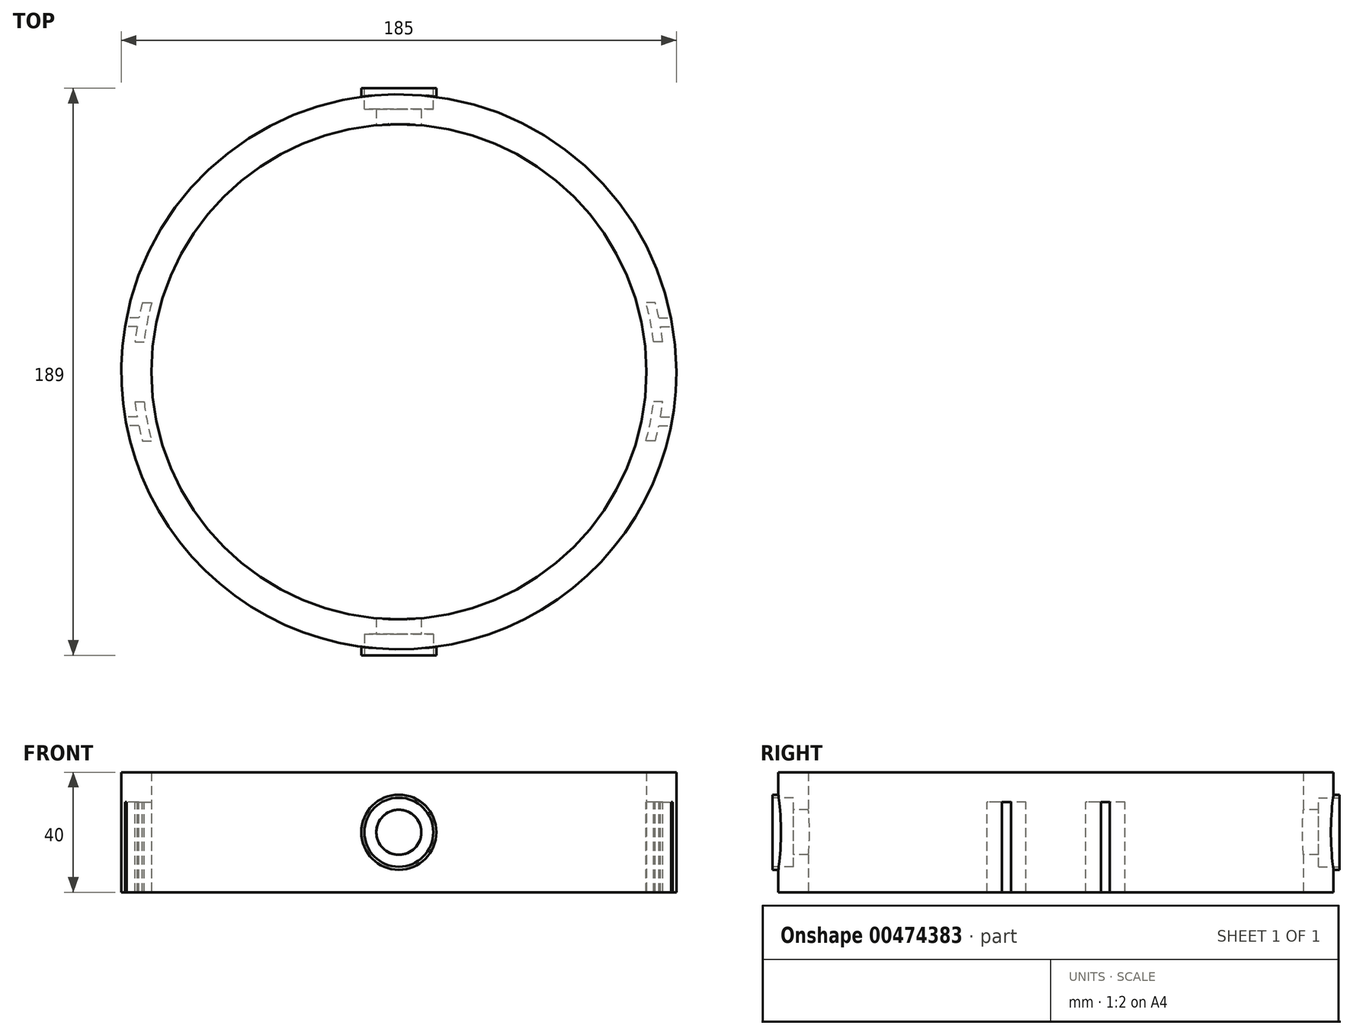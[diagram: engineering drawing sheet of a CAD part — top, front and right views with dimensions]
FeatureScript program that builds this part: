
annotation { "Feature Type Name" : "Feature", "Feature Type Description" : "" }
export const myFeature = defineFeature(function(context is Context, id is Id, definition is map)
    precondition{}
    {
        {
            var Q0;
            Q0=qCreatedBy(makeId("Top.planeOp"),FACE);
            var sketch = newSketch(context, id + "F0", { "sketchPlane" : qUnion([Q0])});
            skCircle(sketch, "E0", {"center": v(0, 0) * mm, "radius": 82.5 * mm});
            skCircle(sketch, "E1", {"center": v(0, 0) * mm, "radius": 92.5 * mm});
            skSolve(sketch);
        }
        {
            var Q0;
            Q0 = qSketchRegion(id + "F0", true);
            extrude(context, id + "F1", {"entities" : qUnion([Q0]), "depth" : 20 * mm, "hasSecondDirection" : true, "secondDirectionOppositeDirection" : true, "secondDirectionDepth" : 20 * mm});
        }
        {
            var Q0;
            Q0=qCreatedBy(makeId("Front.planeOp"),FACE);
            var sketch = newSketch(context, id + "F2", { "sketchPlane" : qUnion([Q0])});
            skCircle(sketch, "E2", {"center": v(0, 0) * mm, "radius": 7.5 * mm});
            skSolve(sketch);
        }
        {
            var Q0;
            Q0 = qSketchRegion(id + "F2", true);
            extrude(context, id + "F3", {"entities" : qUnion([Q0]), "operationType" : NewBodyOperationType.REMOVE, "endBound" : BoundingType.THROUGH_ALL, "oppositeDirection" : true, "depth" : 25 * mm, "hasSecondDirection" : true, "secondDirectionBound" : SecondDirectionBoundingType.THROUGH_ALL, "secondDirectionOppositeDirection" : false, "secondDirectionDepth" : 25 * mm});
        }
        {
            var Q0;
            Q0=qCreatedBy(makeId("Front.planeOp"),FACE);
            cPlane(context, id + "F4", {"entities" : qUnion([Q0]), "cplaneType" : CPlaneType.OFFSET, "offset" : 185 / 2 * mm, "width" : 150 * mm, "height" : 150 * mm});
        }
        {
            var Q0;
            Q0=qCreatedBy(id+"F4.planeOp",FACE);
            var sketch = newSketch(context, id + "F5", { "sketchPlane" : qUnion([Q0])});
            skCircle(sketch, "E3", {"center": v(0, 0) * mm, "radius": 11.5 * mm});
            skSolve(sketch);
        }
        {
            var Q0;
            Q0 = qSketchRegion(id + "F5", true);
            extrude(context, id + "F6", {"entities" : qUnion([Q0]), "operationType" : NewBodyOperationType.REMOVE, "oppositeDirection" : true, "depth" : 5 * mm});
        }
        {
            var Q0;
            Q0=qCreatedBy(makeId("Front.planeOp"),FACE);
            cPlane(context, id + "F7", {"entities" : qUnion([Q0]), "cplaneType" : CPlaneType.OFFSET, "offset" : (185 / 2) * mm, "oppositeDirection" : true, "width" : 150 * mm, "height" : 150 * mm});
        }
        {
            var Q0;
            Q0=qCreatedBy(id+"F7.planeOp",FACE);
            var sketch = newSketch(context, id + "F8", { "sketchPlane" : qUnion([Q0])});
            skCircle(sketch, "E4", {"center": v(0, 0) * mm, "radius": 11.5 * mm});
            skSolve(sketch);
        }
        {
            var Q0;
            Q0 = qSketchRegion(id + "F8", true);
            extrude(context, id + "F9", {"entities" : qUnion([Q0]), "operationType" : NewBodyOperationType.REMOVE, "depth" : 5 * mm});
        }
        {
            var Q0;
            Q0=qCreatedBy(id+"F4.planeOp",FACE);
            var sketch = newSketch(context, id + "F10", { "sketchPlane" : qUnion([Q0])});
            skCircle(sketch, "E5.0", {"center": v(0, 0) * mm, "radius": 11.5 * mm});
            skCircle(sketch, "E6", {"center": v(0, 0) * mm, "radius": 12.5 * mm});
            skSolve(sketch);
        }
        {
            var Q0;
            Q0 = qSketchRegion(id + "F10", true);
            var Q1;
            Q1=makeQuery(id+"F1.opExtrude","SWEPT_FACE",FACE,{"disambiguationData":[OSD([sQuery(id+"F0.wireOp",EDGE,"E1")])]});
            extrude(context, id + "F11", {"entities" : qUnion([Q0]), "operationType" : NewBodyOperationType.ADD, "depth" : 2 * mm, "hasSecondDirection" : true, "secondDirectionBound" : SecondDirectionBoundingType.UP_TO_SURFACE, "secondDirectionOppositeDirection" : true, "secondDirectionBoundEntityFace" : qUnion([Q1]), "secondDirectionDepth" : 25 * mm});
        }
        {
            var Q0;
            Q0=qCreatedBy(id+"F7.planeOp",FACE);
            var sketch = newSketch(context, id + "F12", { "sketchPlane" : qUnion([Q0])});
            skCircle(sketch, "E7", {"center": v(0, 0) * mm, "radius": 12.5 * mm});
            skCircle(sketch, "E8.0", {"center": v(0, 0) * mm, "radius": 11.5 * mm});
            skSolve(sketch);
        }
        {
            var Q0;
            Q0 = qSketchRegion(id + "F12", true);
            extrude(context, id + "F13", {"entities" : qUnion([Q0]), "operationType" : NewBodyOperationType.ADD, "oppositeDirection" : true, "depth" : 2 * mm, "hasSecondDirection" : true, "secondDirectionBound" : SecondDirectionBoundingType.UP_TO_NEXT, "secondDirectionOppositeDirection" : false, "secondDirectionDepth" : 25 * mm});
        }
        {
            var Q0;
            Q0=qCreatedBy(makeId("Top.planeOp"),FACE);
            var sketch = newSketch(context, id + "F14", { "sketchPlane" : qUnion([Q0])});
            skArc(sketch, "E9.0", {"start": v(-91.28, -15) * mm, "mid": v(-91.02, -16.5) * mm, "end": v(-90.73, -18) * mm});
            skCircle(sketch, "E10.0", {"center": v(0, 0) * mm, "radius": 82.5 * mm, "construction": true});
            skArc(sketch, "E11", {"start": v(-86.65, -18) * mm, "mid": v(-86.1, -20.5) * mm, "end": v(-85.46, -23) * mm});
            skArc(sketch, "E12", {"start": v(-84.91, -10) * mm, "mid": v(-83.88, -16.55) * mm, "end": v(-82.35, -23) * mm});
            skLineSegment(sketch, "E13", {"start": v(0, 0) * mm, "end": v(-131.44, 0) * mm, "construction": true});
            skLineSegment(sketch, "E14", {"start": v(-86.65, -18) * mm, "end": v(-90.73, -18) * mm});
            skLineSegment(sketch, "E15", {"start": v(-87.22, -15) * mm, "end": v(-91.28, -15) * mm});
            skLineSegment(sketch, "E16.MirrorCS", {"start": v(-86.65, 18) * mm, "end": v(-90.73, 18) * mm});
            skLineSegment(sketch, "E17.MirrorCS", {"start": v(-87.22, 15) * mm, "end": v(-91.28, 15) * mm});
            skLineSegment(sketch, "E18", {"start": v(-85.46, -23) * mm, "end": v(-82.35, -23) * mm});
            skLineSegment(sketch, "E19", {"start": v(-87.93, -10) * mm, "end": v(-84.91, -10) * mm});
            skLineSegment(sketch, "E20.MirrorCS", {"start": v(-87.93, 10) * mm, "end": v(-84.91, 10) * mm});
            skLineSegment(sketch, "E21.MirrorCS", {"start": v(-85.46, 23) * mm, "end": v(-82.35, 23) * mm});
            skArc(sketch, "E22.trimOffspring", {"start": v(-87.22, 15) * mm, "mid": v(-87.61, 12.5) * mm, "end": v(-87.93, 10) * mm});
            skArc(sketch, "E23.trimOffspring", {"start": v(-87.93, -10) * mm, "mid": v(-87.61, -12.5) * mm, "end": v(-87.22, -15) * mm});
            skArc(sketch, "E24.trimOffspring", {"start": v(-82.35, 23) * mm, "mid": v(-83.88, 16.55) * mm, "end": v(-84.91, 10) * mm});
            skArc(sketch, "E25.trimOffspring", {"start": v(-85.46, 23) * mm, "mid": v(-86.1, 20.5) * mm, "end": v(-86.65, 18) * mm});
            skLineSegment(sketch, "E26.1.0", {"start": v(86.65, 18) * mm, "end": v(90.73, 18) * mm});
            skLineSegment(sketch, "E26.1.1", {"start": v(85.46, 23) * mm, "end": v(82.35, 23) * mm});
            skArc(sketch, "E26.1.2", {"start": v(84.91, 10) * mm, "mid": v(83.88, 16.55) * mm, "end": v(82.35, 23) * mm});
            skArc(sketch, "E26.1.3", {"start": v(87.93, 10) * mm, "mid": v(87.61, 12.5) * mm, "end": v(87.22, 15) * mm});
            skLineSegment(sketch, "E26.1.4", {"start": v(87.93, 10) * mm, "end": v(84.91, 10) * mm});
            skLineSegment(sketch, "E26.1.5", {"start": v(87.22, 15) * mm, "end": v(91.28, 15) * mm});
            skLineSegment(sketch, "E26.1.6", {"start": v(87.93, -10) * mm, "end": v(84.91, -10) * mm});
            skArc(sketch, "E26.1.7", {"start": v(87.22, -15) * mm, "mid": v(87.61, -12.5) * mm, "end": v(87.93, -10) * mm});
            skArc(sketch, "E26.1.8", {"start": v(82.35, -23) * mm, "mid": v(83.88, -16.55) * mm, "end": v(84.91, -10) * mm});
            skLineSegment(sketch, "E26.1.9", {"start": v(85.46, -23) * mm, "end": v(82.35, -23) * mm});
            skArc(sketch, "E26.1.10", {"start": v(85.46, -23) * mm, "mid": v(86.1, -20.5) * mm, "end": v(86.65, -18) * mm});
            skLineSegment(sketch, "E26.1.11", {"start": v(86.65, -18) * mm, "end": v(90.73, -18) * mm});
            skLineSegment(sketch, "E26.1.12", {"start": v(87.22, -15) * mm, "end": v(91.28, -15) * mm});
            skArc(sketch, "E26.1.13", {"start": v(86.65, 18) * mm, "mid": v(86.1, 20.5) * mm, "end": v(85.46, 23) * mm});
            skArc(sketch, "E27.trimOffspring", {"start": v(-90.73, 18) * mm, "mid": v(-91.02, 16.5) * mm, "end": v(-91.28, 15) * mm});
            skArc(sketch, "E28.trimOffspring", {"start": v(90.73, -18) * mm, "mid": v(91.02, -16.5) * mm, "end": v(91.28, -15) * mm});
            skArc(sketch, "E29.trimOffspring", {"start": v(91.28, 15) * mm, "mid": v(91.02, 16.5) * mm, "end": v(90.73, 18) * mm});
            skSolve(sketch);
        }
        {
            var Q0;
            Q0 = qSketchRegion(id + "F14", true);
            extrude(context, id + "F15", {"entities" : qUnion([Q0]), "operationType" : NewBodyOperationType.REMOVE, "endBound" : BoundingType.THROUGH_ALL, "oppositeDirection" : true, "depth" : 25 * mm, "hasSecondDirection" : true, "secondDirectionOppositeDirection" : false, "secondDirectionDepth" : 10 * mm});
        }
    });
